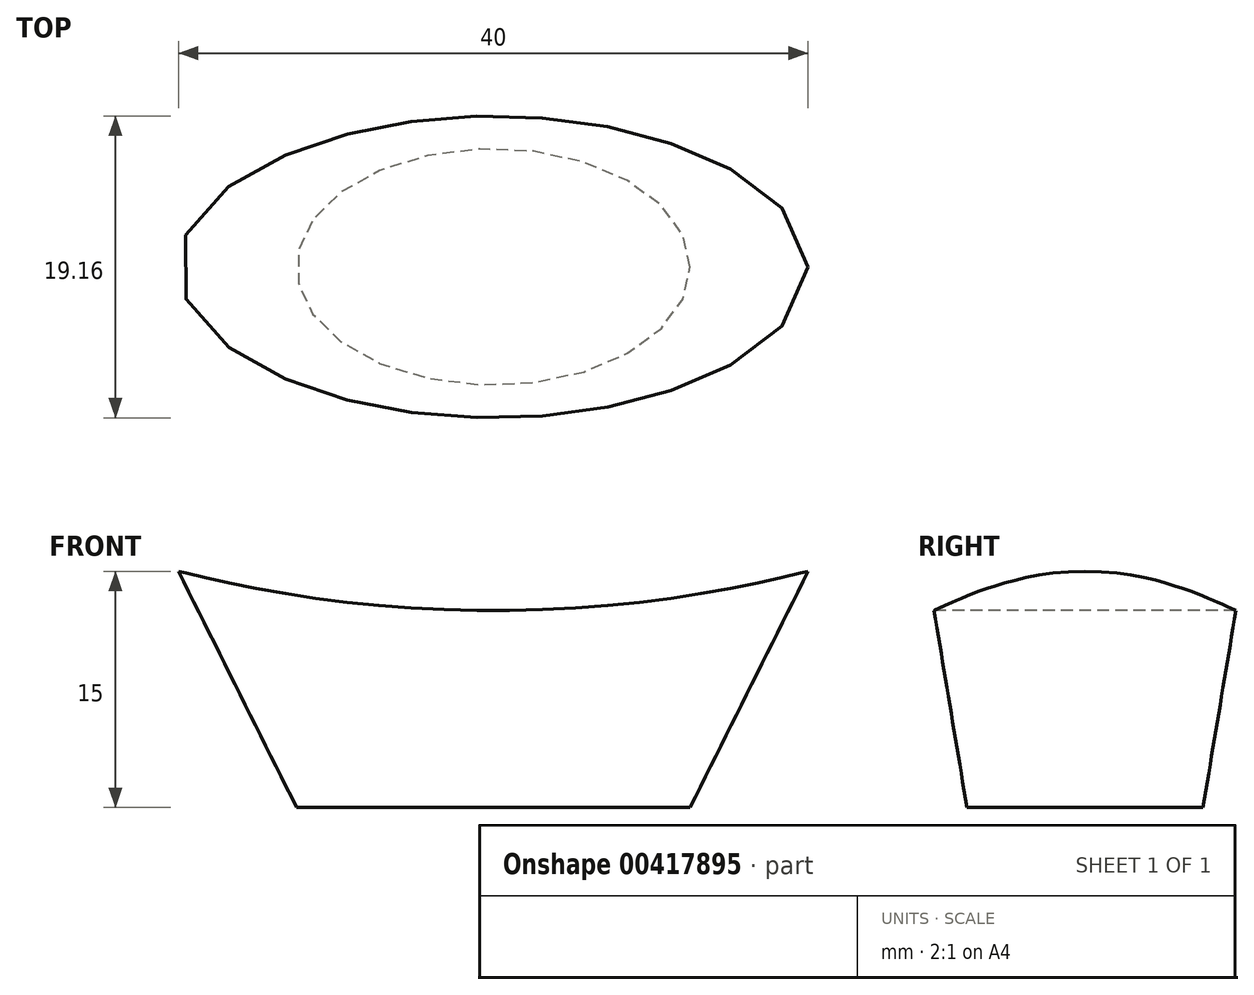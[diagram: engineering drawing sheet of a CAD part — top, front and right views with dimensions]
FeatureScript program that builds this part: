
annotation { "Feature Type Name" : "Feature", "Feature Type Description" : "" }
export const myFeature = defineFeature(function(context is Context, id is Id, definition is map)
    precondition{}
    {
        {
            var Q0;
            Q0=qCreatedBy(makeId("Top.planeOp"),FACE);
            var sketch = newSketch(context, id + "F0", { "sketchPlane" : qUnion([Q0])});
            skEllipse(sketch, "E0", {"center": v(0, 0) * mm, "majorRadius": 12.5 * mm, "minorRadius": 7.5 * mm, "majorAxis": v(1, 0)});
            skSolve(sketch);
        }
        {
            var Q0;
            Q0=qCreatedBy(makeId("Top.planeOp"),FACE);
            cPlane(context, id + "F1", {"entities" : qUnion([Q0]), "cplaneType" : CPlaneType.OFFSET, "offset" : 15 * mm, "width" : 150 * mm, "height" : 150 * mm});
        }
        {
            var Q0;
            Q0=qCreatedBy(id+"F1.planeOp",FACE);
            var sketch = newSketch(context, id + "F2", { "sketchPlane" : qUnion([Q0])});
            skEllipse(sketch, "E1", {"center": v(0, 0) * mm, "majorRadius": 20 * mm, "minorRadius": 10 * mm, "majorAxis": v(1, 0)});
            skSolve(sketch);
        }
        {
            var Q0;
            Q0=makeQuery(id+"F2.imprint","IMPRINT",FACE,{"disambiguationData":[TD([[makeQuery(id+"F2.imprint","IMPRINT",EDGE,{"derivedFrom":sQuery(id+"F2.wireOp",EDGE,"E1")}),1.0]])]});
            var Q1;
            Q1=makeQuery(id+"F0.imprint","IMPRINT",FACE,{"disambiguationData":[TD([[makeQuery(id+"F0.imprint","IMPRINT",EDGE,{"derivedFrom":sQuery(id+"F0.wireOp",EDGE,"E0")}),1.0]])]});
            loft(context, id + "F3", {"sheetProfilesArray" : [{ "sheetProfileEntities" : qUnion([Q0]) }, { "sheetProfileEntities" : qUnion([Q1]) }]});
        }
        {
            var Q0;
            Q0=qCreatedBy(makeId("Front.planeOp"),FACE);
            var sketch = newSketch(context, id + "F4", { "sketchPlane" : qUnion([Q0])});
            skArc(sketch, "E2", {"start": v(-20, 15) * mm, "mid": v(0, 12.5) * mm, "end": v(20, 15) * mm});
            skLineSegment(sketch, "E3.bottom", {"start": v(-20, 15) * mm, "end": v(20, 15) * mm});
            skSolve(sketch);
        }
        {
            var Q0;
            Q0 = qSketchRegion(id + "F4", true);
            extrude(context, id + "F5", {"entities" : qUnion([Q0]), "operationType" : NewBodyOperationType.REMOVE, "endBound" : BoundingType.SYMMETRIC, "oppositeDirection" : true, "depth" : 28 * mm});
        }
        {
            var Q0;
            Q0=qCreatedBy(makeId("Top.planeOp"),FACE);
            cPlane(context, id + "F6", {"entities" : qUnion([Q0]), "cplaneType" : CPlaneType.OFFSET, "offset" : 12 * mm, "width" : 150 * mm, "height" : 150 * mm});
        }
        {
            var Q0;
            Q0=qCreatedBy(id+"F6.planeOp",FACE);
            var sketch = newSketch(context, id + "F7", { "sketchPlane" : qUnion([Q0])});
            skEllipticalArc(sketch, "E4", {});
            skLineSegment(sketch, "E5", {"start": v(-14.18, 0) * mm, "end": v(13.46, 0) * mm, "construction": true});
            skPoint(sketch, "E5.startSnap0", {"position": v(-10, 0) * mm});
            const initialGuessF7  = {"E4": [0, 0, 1, 0, 0.01, 0.0075, 0, 3.141592653589793]};
            skSetInitialGuess(sketch, initialGuessF7);
            skSolve(sketch);
        }
        {
            var Q0;
            Q0=qCreatedBy(id+"F6.planeOp",FACE);
            var sketch = newSketch(context, id + "F8", { "sketchPlane" : qUnion([Q0])});
            skEllipticalArc(sketch, "E6", {});
            skLineSegment(sketch, "E7", {"start": v(-12.55, 0) * mm, "end": v(11.88, 0) * mm, "construction": true});
            const initialGuessF8  = {"E6": [0, 0, 1, 0, 0.010234562214463953, 0.0075, 3.141592653589793, 0]};
            skSetInitialGuess(sketch, initialGuessF8);
            skSolve(sketch);
        }
        {
            var Q0;
            Q0=qCreatedBy(makeId("Front.planeOp"),FACE);
            var sketch = newSketch(context, id + "F9", { "sketchPlane" : qUnion([Q0])});
            skArc(sketch, "E8", {"start": v(10, 12) * mm, "mid": v(0, 18.77) * mm, "end": v(-10, 12) * mm});
            skSolve(sketch);
        }
        {
            var Q0;
            Q0=qCreatedBy(makeId("Right.planeOp"),FACE);
            var sketch = newSketch(context, id + "F10", { "sketchPlane" : qUnion([Q0])});
            skArc(sketch, "E9", {"start": v(7.5, 12) * mm, "mid": v(0, 18.77) * mm, "end": v(-7.5, 12) * mm});
            skSolve(sketch);
        }
        {
            var Q0;
            Q0=sQuery(id+"F7.wireOp",EDGE,"E4");
            var Q1;
            Q1=sQuery(id+"F9.wireOp",EDGE,"E8");
            var Q2;
            Q2=sQuery(id+"F8.wireOp",EDGE,"E6");
            var Q3;
            Q3=sQuery(id+"F10.wireOp",EDGE,"E9");
            loft(context, id + "F11", {"bodyType" : ToolBodyType.SURFACE, "addGuides" : true, "wireProfilesArray" : [{ "wireProfileEntities" : qUnion([Q0]) }, { "wireProfileEntities" : qUnion([Q1]) }, { "wireProfileEntities" : qUnion([Q2]) }], "guidesArray" : [{ "guideEntities" : qUnion([Q3]), "guideDerivativeType" : LoftGuideDerivativeType.DEFAULT, "guideDerivativeMagnitude" : 1 }]});
        }
    });
